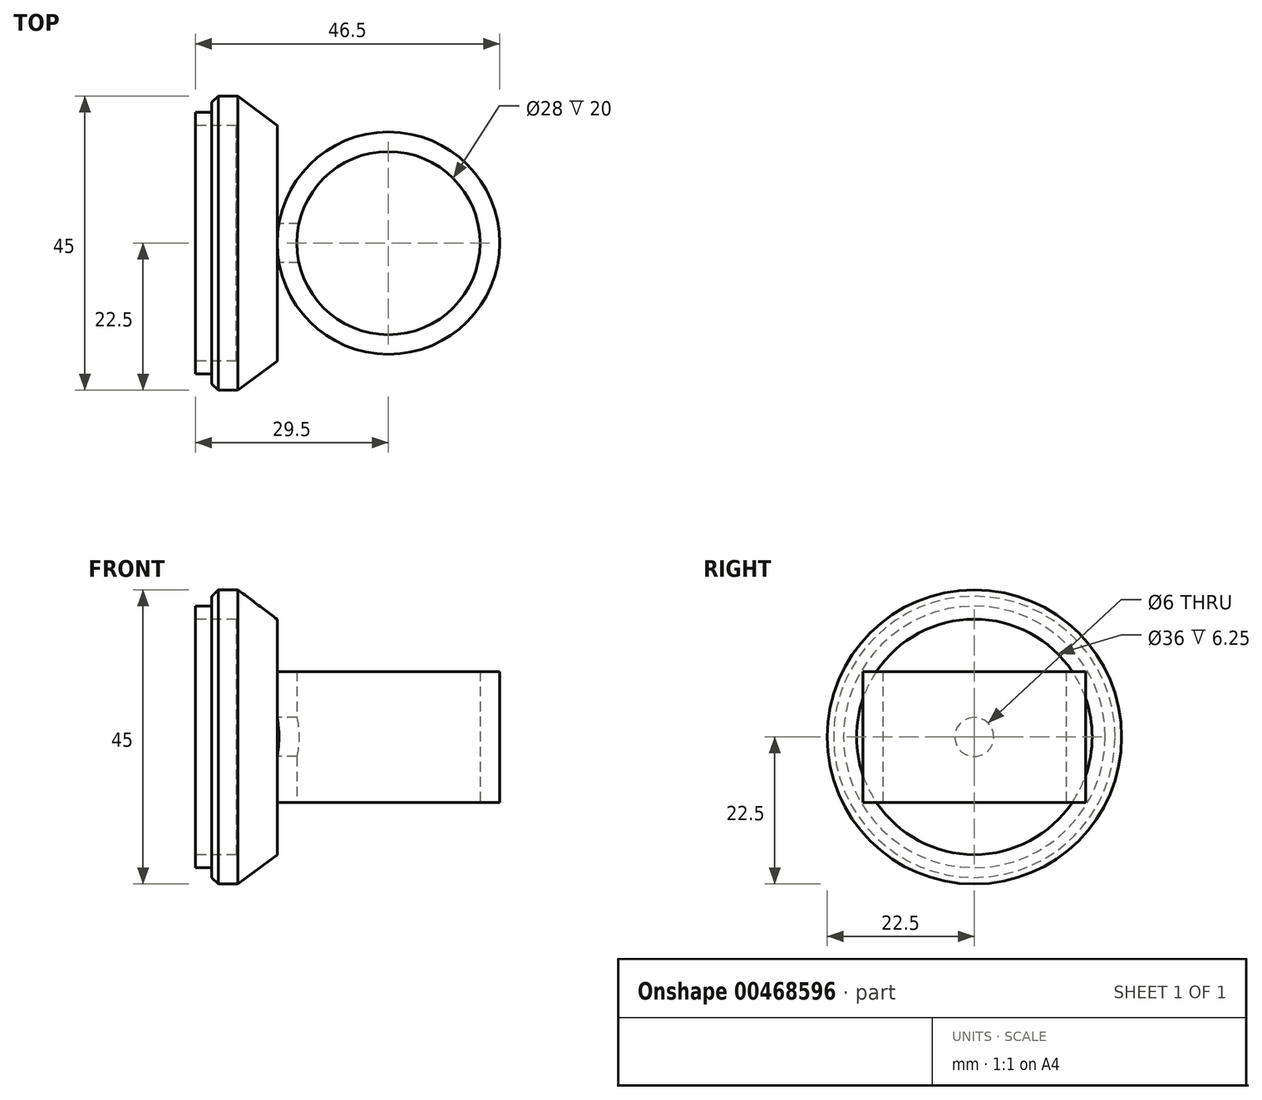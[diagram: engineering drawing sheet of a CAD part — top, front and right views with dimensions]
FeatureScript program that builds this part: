
annotation { "Feature Type Name" : "Feature", "Feature Type Description" : "" }
export const myFeature = defineFeature(function(context is Context, id is Id, definition is map)
    precondition{}
    {
        {
            var Q0;
            Q0=qCreatedBy(makeId("Front.planeOp"),FACE);
            var sketch = newSketch(context, id + "F0", { "sketchPlane" : qUnion([Q0])});
            skLineSegment(sketch, "E0", {"start": v(0, 0) * mm, "end": v(12.5, 0) * mm});
            skPoint(sketch, "E1", {"position": v(0, 20) * mm});
            skLineSegment(sketch, "E2", {"start": v(0, 20) * mm, "end": v(2.5, 20) * mm});
            skLineSegment(sketch, "E3", {"start": v(2.5, 20) * mm, "end": v(2.5, 22.5) * mm});
            skLineSegment(sketch, "E4", {"start": v(12.5, 0) * mm, "end": v(12.5, 18) * mm});
            skLineSegment(sketch, "E5", {"start": v(2.5, 22.5) * mm, "end": v(6.5, 22.5) * mm});
            skLineSegment(sketch, "E6", {"start": v(6.5, 22.5) * mm, "end": v(12.5, 18) * mm});
            skLineSegment(sketch, "E7", {"start": v(12.5, 18) * mm, "end": v(0, 18) * mm});
            skLineSegment(sketch, "E8", {"start": v(0, 18) * mm, "end": v(0, 20) * mm});
            skLineSegment(sketch, "E9", {"start": v(6.25, 0) * mm, "end": v(6.25, 18) * mm});
            skLineSegment(sketch, "E10", {"start": v(12.5, 0) * mm, "end": v(15.5, 0) * mm});
            skLineSegment(sketch, "E11", {"start": v(15.5, 0) * mm, "end": v(15.5, 3) * mm});
            skLineSegment(sketch, "E12", {"start": v(15.5, 3) * mm, "end": v(12.5, 3) * mm});
            skSolve(sketch);
        }
        {
            var Q0;
            Q0=qSketchRegion(id+"F0",true);
            var Q1;
            Q1=sQuery(id+"F0.wireOp",EDGE,"E0");
            revolve(context, id + "F1", {"entities" : qUnion([Q0]), "axis" : qUnion([Q1]), "revolveType" : RevolveType.FULL});
        }
        {
            var Q0;
            Q0=qCreatedBy(makeId("Top.planeOp"),FACE);
            var sketch = newSketch(context, id + "F2", { "sketchPlane" : qUnion([Q0])});
            skPoint(sketch, "E13", {"position": v(29.5, 0) * mm});
            skCircle(sketch, "E14", {"center": v(29.5, 0) * mm, "radius": 17 * mm});
            skCircle(sketch, "E15", {"center": v(29.5, 0) * mm, "radius": 14 * mm});
            skSolve(sketch);
        }
        {
            var Q0;
            Q0=qSketchRegion(id+"F2",true);
            extrude(context, id + "F3", {"entities" : qUnion([Q0]), "depth" : 20 * mm, "symmetric" : true});
        }
        {
            var Q0;
            Q0=makeQuery(id+"F1.opRevolve","SWEPT_FACE",FACE,{"disambiguationData":[OSD([sQuery(id+"F0.wireOp",EDGE,"E4")])]});
            var sketch = newSketch(context, id + "F4", { "sketchPlane" : qUnion([Q0])});
            skCircle(sketch, "E16.0", {"center": v(0, 0) * mm, "radius": 3 * mm});
            skSolve(sketch);
        }
        {
            var Q0;
            Q0=qSketchRegion(id+"F4",true);
            extrude(context, id + "F5", {"entities" : qUnion([Q0]), "operationType" : NewBodyOperationType.REMOVE, "depth" : 5 * mm});
        }
        {
            var Q0;
            Q0=makeQuery(id+"F1.opRevolve","SWEPT_EDGE",EDGE,{"disambiguationData":[OSD([sQuery(id+"F0.wireOp",EDGE,"E3"),sQuery(id+"F0.wireOp",EDGE,"E5")])]});
            chamfer(context, id + "F6", {"entities" : qUnion([Q0]), "width" : 1 * mm, "tangentPropagation" : true});
        }
    });
